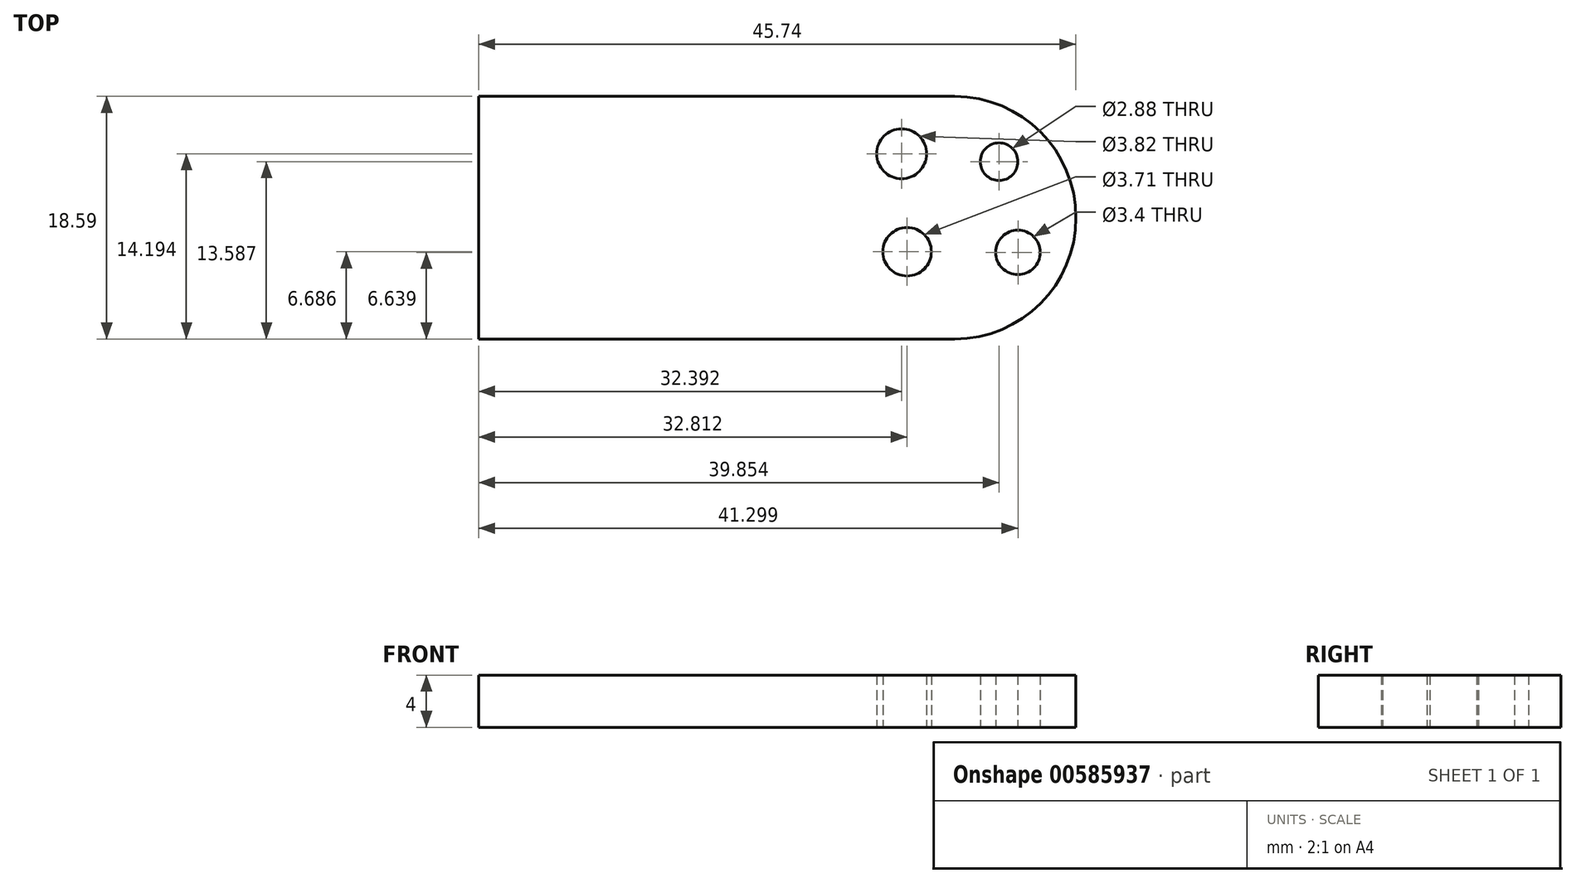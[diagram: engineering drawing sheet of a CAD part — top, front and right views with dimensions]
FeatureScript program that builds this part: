
annotation { "Feature Type Name" : "Feature", "Feature Type Description" : "" }
export const myFeature = defineFeature(function(context is Context, id is Id, definition is map)
    precondition{}
    {
        {
            var Q0;
            Q0=qCreatedBy(makeId("Top.planeOp"),FACE);
            var sketch = newSketch(context, id + "F0", { "sketchPlane" : qUnion([Q0])});
            skLineSegment(sketch, "E0.bottom", {"start": v(0, 0) * mm, "end": v(36.45, 0) * mm});
            skLineSegment(sketch, "E0.top", {"start": v(0, 18.59) * mm, "end": v(36.45, 18.59) * mm});
            skLineSegment(sketch, "E0.left", {"start": v(0, 0) * mm, "end": v(0, 18.59) * mm});
            skLineSegment(sketch, "E0.right", {"start": v(36.45, 0) * mm, "end": v(36.45, 18.59) * mm});
            skArc(sketch, "E1", {"start": v(36.45, 0) * mm, "mid": v(45.74, 9.3) * mm, "end": v(36.45, 18.59) * mm});
            skCircle(sketch, "E2", {"center": v(39.85, 13.59) * mm, "radius": 1.44 * mm});
            skCircle(sketch, "E3", {"center": v(41.3, 6.64) * mm, "radius": 1.7 * mm});
            skCircle(sketch, "E4", {"center": v(32.4, 14.2) * mm, "radius": 1.91 * mm});
            skCircle(sketch, "E5", {"center": v(32.81, 6.69) * mm, "radius": 1.86 * mm});
            skSolve(sketch);
        }
        {
            var Q0;
            Q0 = qSketchRegion(id + "F0", true);
            extrude(context, id + "F1", {"entities" : qUnion([Q0]), "depth" : 4 * mm, "offsetDistance" : 25.4 * mm});
        }
    });
